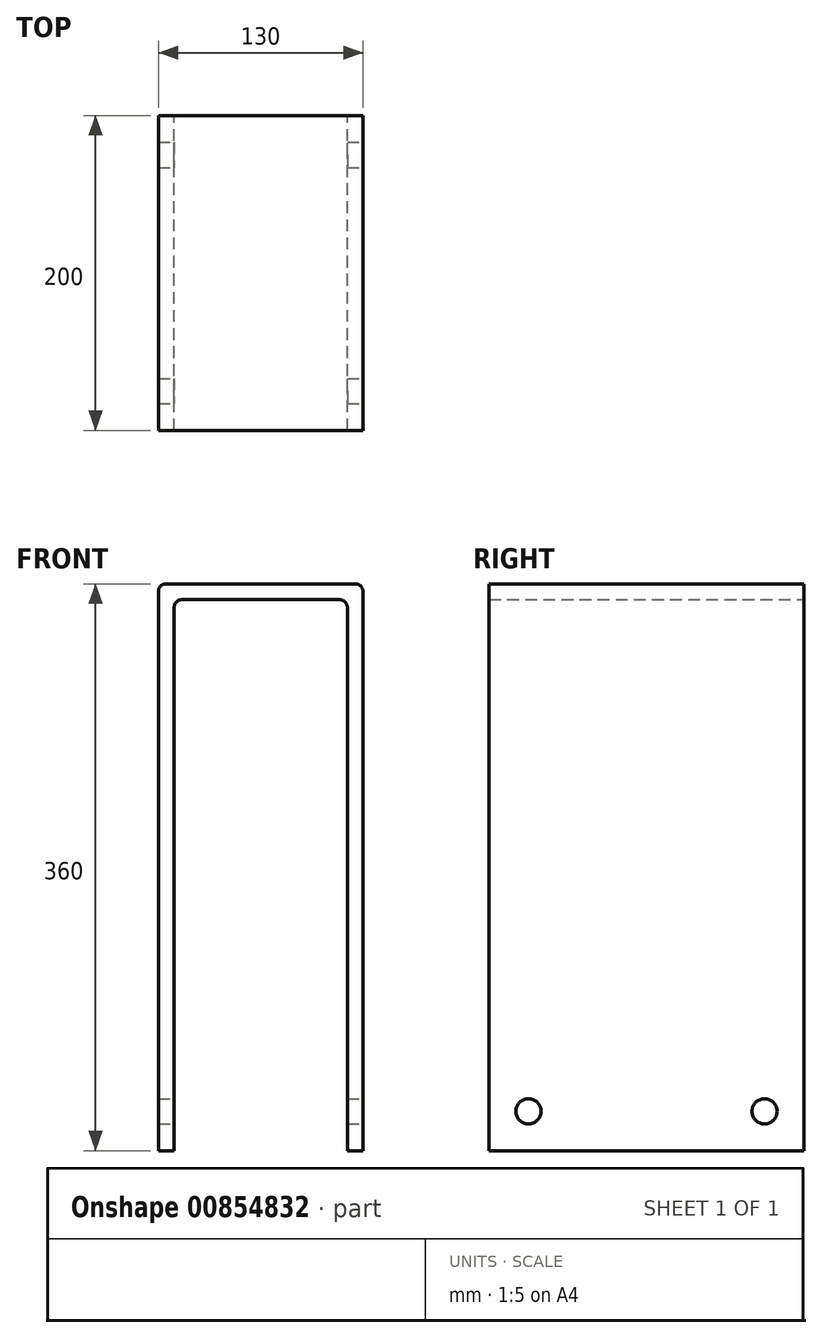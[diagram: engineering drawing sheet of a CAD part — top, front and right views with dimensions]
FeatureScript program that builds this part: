
annotation { "Feature Type Name" : "Feature", "Feature Type Description" : "" }
export const myFeature = defineFeature(function(context is Context, id is Id, definition is map)
    precondition{}
    {
        {
            var Q0;
            Q0=qCreatedBy(makeId("Front.planeOp"),FACE);
            var sketch = newSketch(context, id + "F0", { "sketchPlane" : qUnion([Q0])});
            skLineSegment(sketch, "E0", {"start": v(0, 0) * mm, "end": v(0, 360) * mm});
            skLineSegment(sketch, "E1", {"start": v(0, 360) * mm, "end": v(130, 360) * mm});
            skLineSegment(sketch, "E2", {"start": v(130, 360) * mm, "end": v(130, 0) * mm});
            skLineSegment(sketch, "E3", {"start": v(130, 0) * mm, "end": v(120, 0) * mm});
            skLineSegment(sketch, "E4", {"start": v(120, 0) * mm, "end": v(120, 350) * mm});
            skLineSegment(sketch, "E5", {"start": v(120, 350) * mm, "end": v(10, 350) * mm});
            skLineSegment(sketch, "E6", {"start": v(10, 350) * mm, "end": v(10, 0) * mm});
            skLineSegment(sketch, "E7", {"start": v(10, 0) * mm, "end": v(0, 0) * mm});
            skSolve(sketch);
        }
        {
            var Q0;
            Q0 = qSketchRegion(id + "F0", true);
            extrude(context, id + "F1", {"entities" : qUnion([Q0]), "depth" : 200 * mm, "offsetDistance" : 25 * mm});
        }
        {
            var Q0;
            Q0=makeQuery(id+"F1.opExtrude","SWEPT_EDGE",EDGE,{"disambiguationData":[OSD([sQuery(id+"F0.wireOp",EDGE,"E1"),sQuery(id+"F0.wireOp",EDGE,"E2")])]});
            var Q1;
            Q1=makeQuery(id+"F1.opExtrude","SWEPT_EDGE",EDGE,{"disambiguationData":[OSD([sQuery(id+"F0.wireOp",EDGE,"E0"),sQuery(id+"F0.wireOp",EDGE,"E1")])]});
            var Q2;
            Q2=makeQuery(id+"F1.opExtrude","SWEPT_EDGE",EDGE,{"disambiguationData":[OSD([sQuery(id+"F0.wireOp",EDGE,"E5"),sQuery(id+"F0.wireOp",EDGE,"E6")])]});
            var Q3;
            Q3=makeQuery(id+"F1.opExtrude","SWEPT_EDGE",EDGE,{"disambiguationData":[OSD([sQuery(id+"F0.wireOp",EDGE,"E4"),sQuery(id+"F0.wireOp",EDGE,"E5")])]});
            fillet(context, id + "F2", {"entities" : qUnion([Q0, Q1, Q2, Q3]), "radius" : 5 * mm, "tangentPropagation" : true, "allowEdgeOverflow" : false});
        }
        {
            var Q0;
            Q0=makeQuery(id+"F1.opExtrude","SWEPT_FACE",FACE,{"disambiguationData":[OSD([sQuery(id+"F0.wireOp",EDGE,"E2")])]});
            var sketch = newSketch(context, id + "F3", { "sketchPlane" : qUnion([Q0])});
            skCircle(sketch, "E8", {"center": v(-25, 25) * mm, "radius": 8 * mm});
            skCircle(sketch, "E9", {"center": v(-175, 25) * mm, "radius": 8 * mm});
            skSolve(sketch);
        }
        {
            var Q0;
            Q0 = qSketchRegion(id + "F3", true);
            extrude(context, id + "F4", {"entities" : qUnion([Q0]), "operationType" : NewBodyOperationType.REMOVE, "oppositeDirection" : true, "depth" : 400 * mm, "offsetDistance" : 25 * mm});
        }
    });
